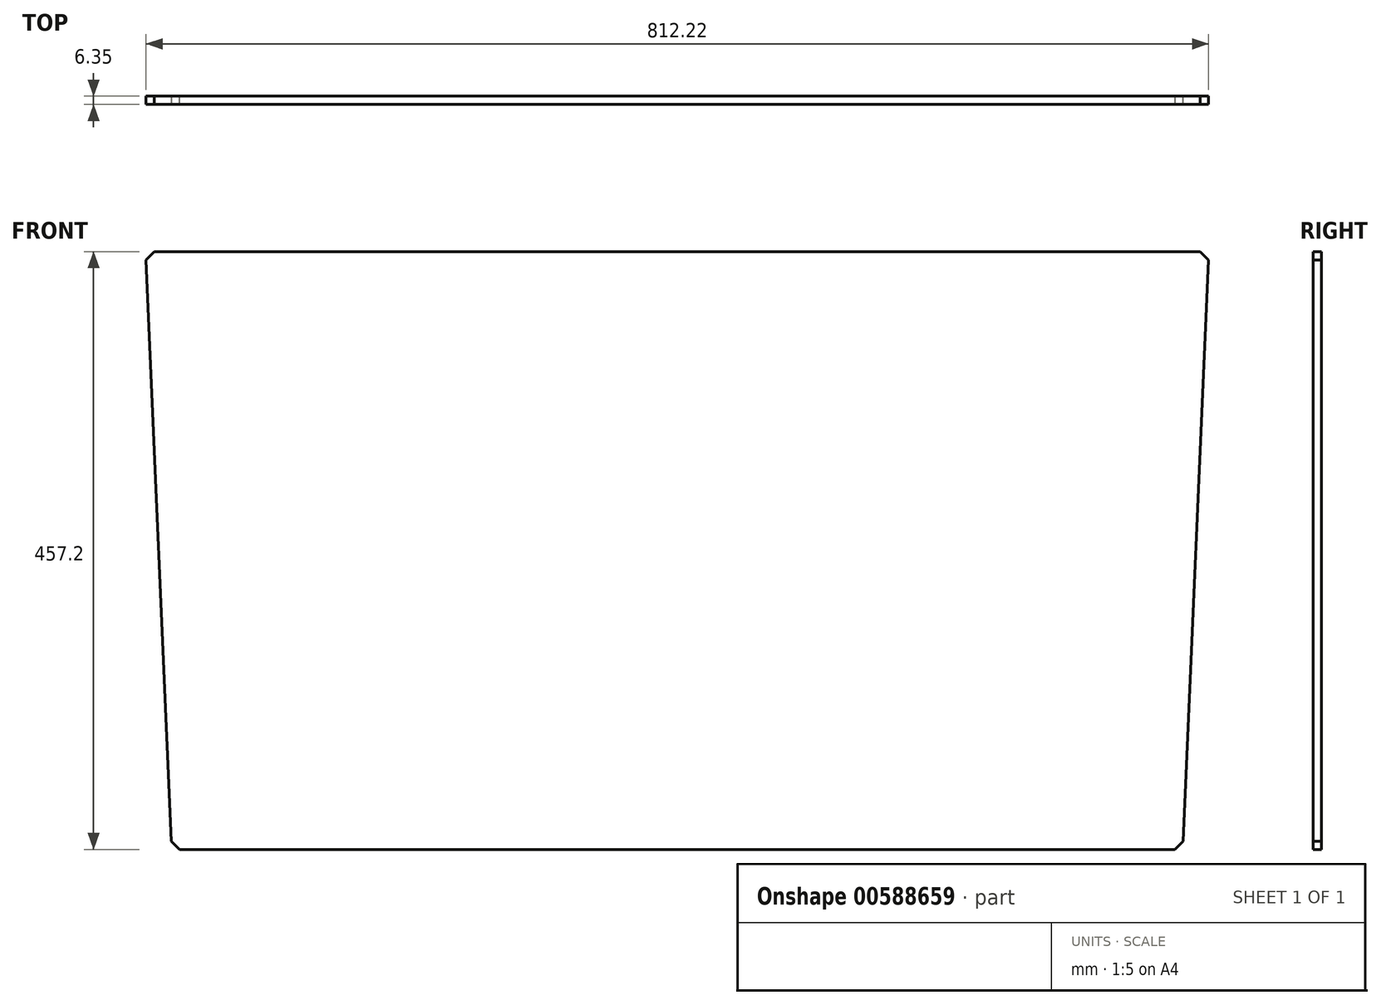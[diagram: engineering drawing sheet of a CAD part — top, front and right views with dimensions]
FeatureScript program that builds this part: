
annotation { "Feature Type Name" : "Feature", "Feature Type Description" : "" }
export const myFeature = defineFeature(function(context is Context, id is Id, definition is map)
    precondition{}
    {
        {
            var Q0;
            Q0=qCreatedBy(makeId("Front.planeOp"),FACE);
            var sketch = newSketch(context, id + "F0", { "sketchPlane" : qUnion([Q0])});
            skLineSegment(sketch, "E0", {"start": v(0, 0) * mm, "end": v(812.8, 0) * mm});
            skLineSegment(sketch, "E1", {"start": v(812.8, 0) * mm, "end": v(792.84, -457.2) * mm});
            skLineSegment(sketch, "E2", {"start": v(792.84, -457.2) * mm, "end": v(19.96, -457.2) * mm});
            skLineSegment(sketch, "E3", {"start": v(19.96, -457.2) * mm, "end": v(0, 0) * mm});
            skSolve(sketch);
        }
        {
            var Q0;
            Q0=makeQuery(id+"F0.imprint","IMPRINT",FACE,{"disambiguationData":[TD([[makeQuery(id+"F0.imprint","IMPRINT",EDGE,{"derivedFrom":sQuery(id+"F0.wireOp",EDGE,"E0")}),-1.0]])]});
            extrude(context, id + "F1", {"entities" : qUnion([Q0]), "depth" : 6.35 * mm, "offsetDistance" : 25.4 * mm});
        }
        {
            var Q0;
            Q0=makeQuery(id+"F1.opExtrude","SWEPT_EDGE",EDGE,{"disambiguationData":[OSD([sQuery(id+"F0.wireOp",EDGE,"E0"),sQuery(id+"F0.wireOp",EDGE,"E1")])]});
            var Q1;
            Q1=makeQuery(id+"F1.opExtrude","SWEPT_EDGE",EDGE,{"disambiguationData":[OSD([sQuery(id+"F0.wireOp",EDGE,"E0"),sQuery(id+"F0.wireOp",EDGE,"E3")])]});
            var Q2;
            Q2=makeQuery(id+"F1.opExtrude","SWEPT_EDGE",EDGE,{"disambiguationData":[OSD([sQuery(id+"F0.wireOp",EDGE,"E2"),sQuery(id+"F0.wireOp",EDGE,"E3")])]});
            var Q3;
            Q3=makeQuery(id+"F1.opExtrude","SWEPT_EDGE",EDGE,{"disambiguationData":[OSD([sQuery(id+"F0.wireOp",EDGE,"E1"),sQuery(id+"F0.wireOp",EDGE,"E2")])]});
            chamfer(context, id + "F2", {"entities" : qUnion([Q0, Q1, Q2, Q3]), "width" : 6.35 * mm, "tangentPropagation" : true});
        }
    });
